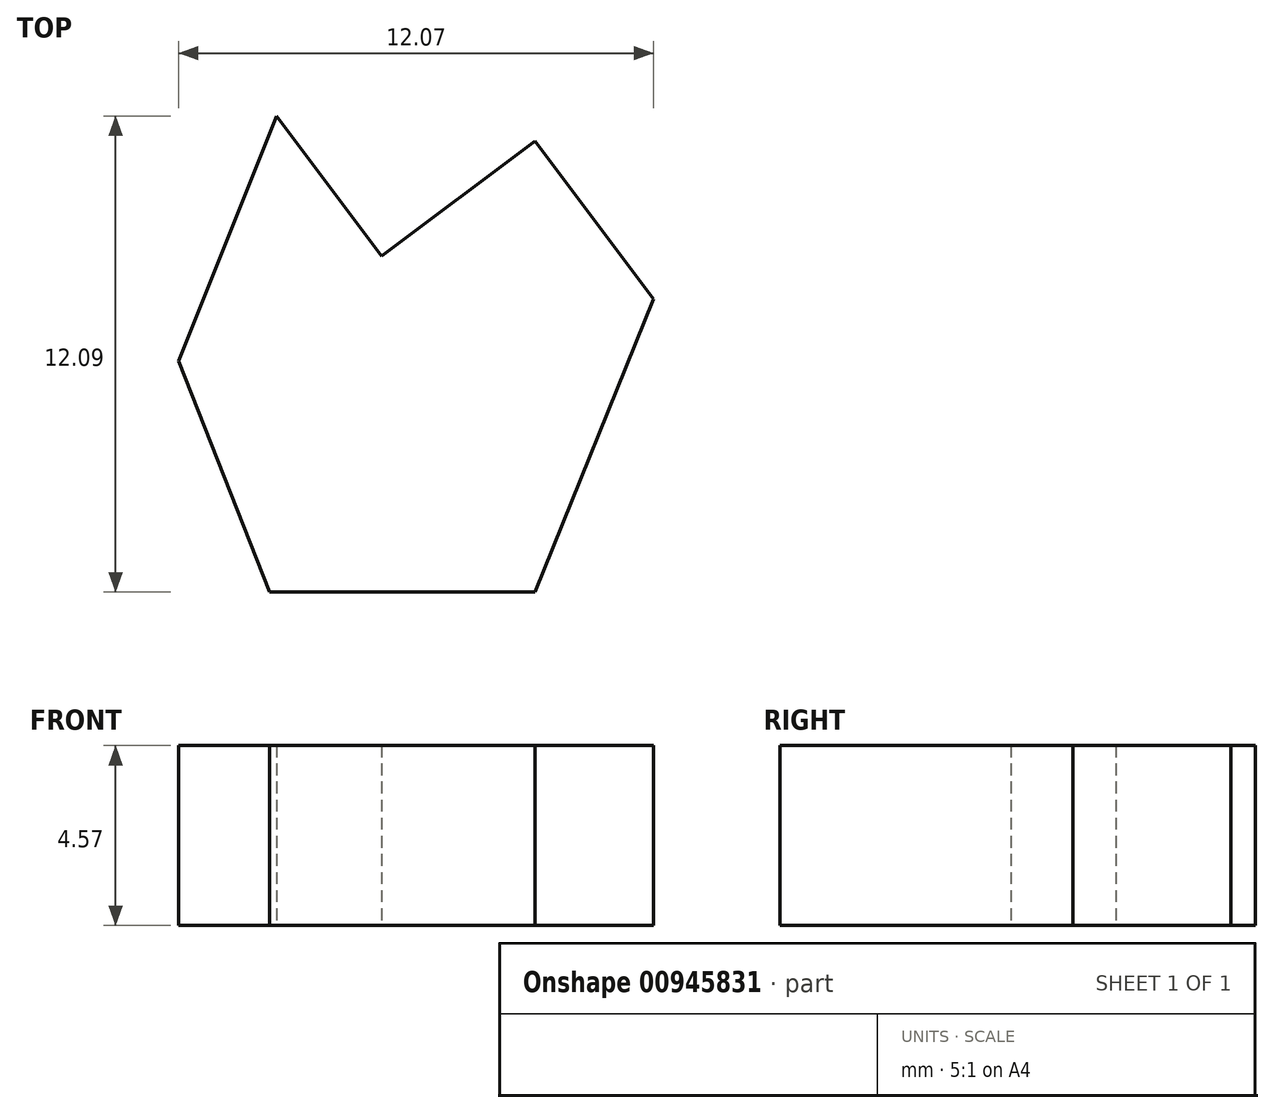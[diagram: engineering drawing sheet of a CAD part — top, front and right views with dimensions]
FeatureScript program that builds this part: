
annotation { "Feature Type Name" : "Feature", "Feature Type Description" : "" }
export const myFeature = defineFeature(function(context is Context, id is Id, definition is map)
    precondition{}
    {
        {
            var Q0;
            Q0=qCreatedBy(makeId("Top.planeOp"),FACE);
            var sketch = newSketch(context, id + "F0", { "sketchPlane" : qUnion([Q0])});
            skLineSegment(sketch, "E0", {"start": v(-62.5, 45.96) * mm, "end": v(-59.83, 42.4) * mm});
            skLineSegment(sketch, "E1", {"start": v(-59.83, 42.4) * mm, "end": v(-55.93, 45.33) * mm});
            skLineSegment(sketch, "E2", {"start": v(-55.93, 45.33) * mm, "end": v(-52.92, 41.32) * mm});
            skLineSegment(sketch, "E3", {"start": v(-52.92, 41.32) * mm, "end": v(-55.93, 33.87) * mm});
            skLineSegment(sketch, "E4", {"start": v(-55.93, 33.87) * mm, "end": v(-62.67, 33.87) * mm});
            skLineSegment(sketch, "E5", {"start": v(-62.67, 33.87) * mm, "end": v(-64.99, 39.74) * mm});
            skLineSegment(sketch, "E6", {"start": v(-64.99, 39.74) * mm, "end": v(-62.5, 45.96) * mm});
            skSolve(sketch);
        }
        {
            var Q0;
            Q0=makeQuery(id+"F0.imprint","IMPRINT",FACE,{"disambiguationData":[TD([[makeQuery(id+"F0.imprint","IMPRINT",EDGE,{"derivedFrom":sQuery(id+"F0.wireOp",EDGE,"E0")}),-1.0]])]});
            extrude(context, id + "F1", {"entities" : qUnion([Q0]), "depth" : 4.57 * mm, "offsetDistance" : 25.4 * mm});
        }
    });
